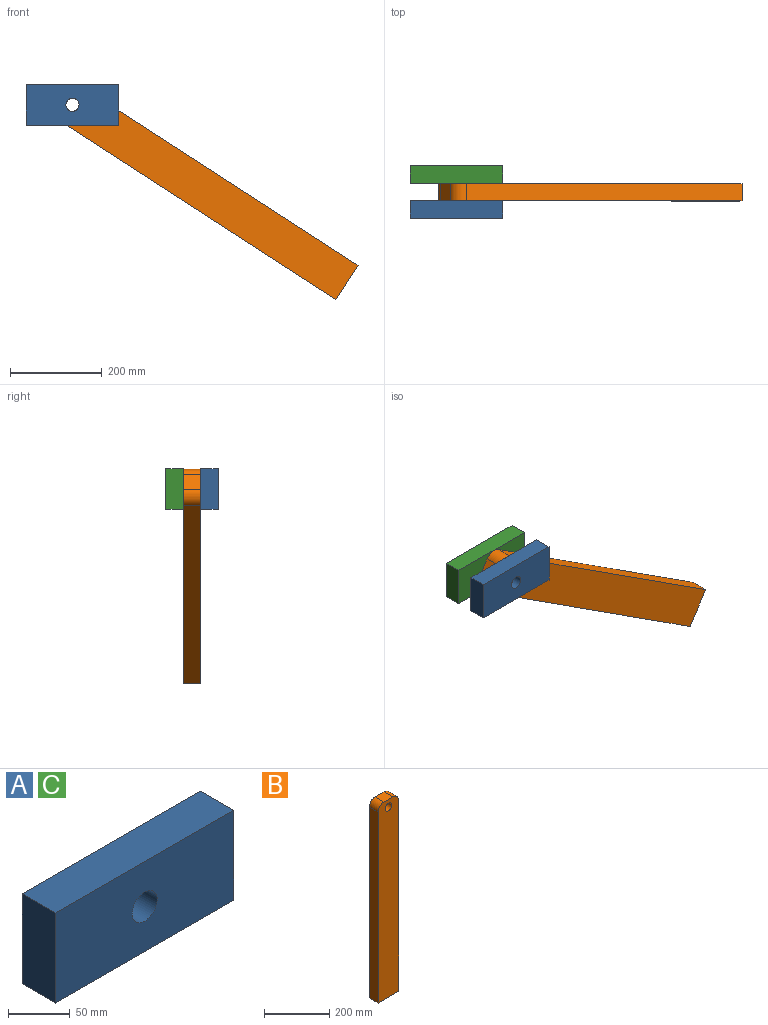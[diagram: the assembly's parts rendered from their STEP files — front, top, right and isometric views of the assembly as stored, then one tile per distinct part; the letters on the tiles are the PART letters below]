
ASSEMBLY  parts=3 mates=5
PART A: 7 faces, bbox 203.2x38.1x88.9 mm
  f0: plane 203.2x38.1mm, normal (0,0,-1), area 7741.9mm2, adj f1,f4,f5,f6
  f1: plane 88.9x38.1mm, normal (1,0,0), area 3387.1mm2, adj f0,f2,f5,f6
  f2: plane 203.2x38.1mm, normal (0,0,1), area 7741.9mm2, adj f1,f4,f5,f6
  f3: cylinder r=14.29mm len=38.1mm, axis (0,1,0), area 3420.3mm2, adj f5,f6
  f4: plane 88.9x38.1mm, normal (-1,0,0), area 3387.1mm2, adj f0,f2,f5,f6
  f5: plane 203.2x88.9mm, normal (0,-1,0), area 17423.2mm2, adj f0,f1,f2,f3,f4
  f6: plane 203.2x88.9mm, normal (0,1,0), area 17423.2mm2, adj f0,f1,f2,f3,f4
PART B: 9 faces, bbox 88.9x38.1x743 mm
  f0: plane 717.55x38.1mm, normal (1,0,0), area 27338.7mm2, adj f3,f5,f6,f7
  f1: plane 38.1x38.1mm, normal (0,0,1), area 1451.6mm2, adj f5,f6,f7,f8
  f2: plane 717.55x38.1mm, normal (-1,0,0), area 27338.7mm2, adj f3,f5,f6,f8
  f3: plane 88.9x38.1mm, normal (0,0,-1), area 3387.1mm2, adj f0,f2,f5,f6
  f4: cylinder r=14.29mm len=38.1mm, axis (0,1,0), area 3420.3mm2, adj f5,f6
  f5: plane 742.95x88.9mm, normal (0,-1,0), area 65130mm2, adj f0,f1,f2,f3,f4,f7,f8
  f6: plane 742.95x88.9mm, normal (0,1,0), area 65130mm2, adj f0,f1,f2,f3,f4,f7,f8
  f7: cylinder r=25.4mm len=38.1mm, axis (0,-1,0), area 1520.1mm2, adj f0,f1,f5,f6
  f8: cylinder r=25.4mm len=38.1mm, axis (0,1,0), area 1520.1mm2, adj f1,f2,f5,f6
PART C: same geometry as A
PLACE A t=(45.01,131.43,35.76)mm fixed
PLACE B rot(axis=(0,-1,0),57.1deg) t=(332.99,169.53,-150.39)mm
PLACE C t=(45.01,207.63,35.76)mm
MATE cylindrical C.f3 <-> B.f4  axis (0,-1,0) through (45.01,169.53,35.76)mm
MATE planar A.f3 <-> B.f5  axis (0,1,0) through (45.01,131.43,35.76)mm
MATE planar A.f2 <-> C.f2  axis (0,0,1) through (45.01,112.38,80.21)mm
MATE planar C.f5 <-> B.f6  axis (0,-1,0) through (45.01,169.53,-8.69)mm
MATE cylindrical B.f4 <-> A.f3  axis (0,-1,0) through (45.01,131.43,35.76)mm
